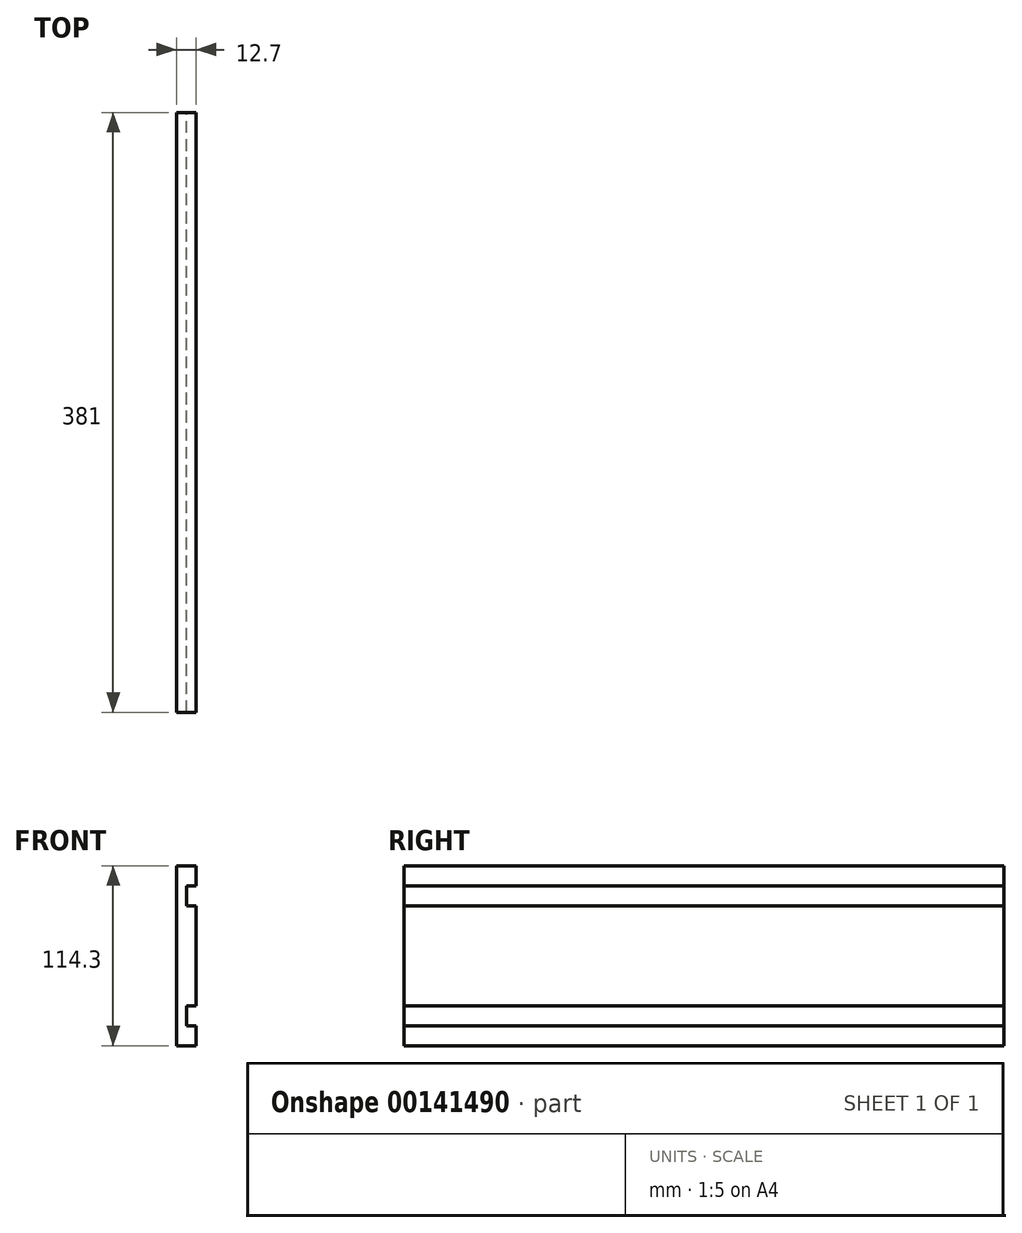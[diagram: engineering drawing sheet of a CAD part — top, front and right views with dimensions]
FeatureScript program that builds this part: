
annotation { "Feature Type Name" : "Feature", "Feature Type Description" : "" }
export const myFeature = defineFeature(function(context is Context, id is Id, definition is map)
    precondition{}
    {
        {
            var Q0;
            Q0=qCreatedBy(makeId("Front.planeOp"),FACE);
            var sketch = newSketch(context, id + "F0", { "sketchPlane" : qUnion([Q0])});
            skLineSegment(sketch, "E0.bottom", {"start": v(0, 114.3) * mm, "end": v(12.7, 114.3) * mm});
            skLineSegment(sketch, "E0.top", {"start": v(0, 0) * mm, "end": v(12.7, 0) * mm});
            skLineSegment(sketch, "E0.left", {"start": v(0, 114.3) * mm, "end": v(0, 0) * mm});
            skLineSegment(sketch, "E0.right", {"start": v(12.7, 114.3) * mm, "end": v(12.7, 101.6) * mm});
            skLineSegment(sketch, "E1.bottom", {"start": v(12.7, 25.4) * mm, "end": v(6.35, 25.4) * mm});
            skLineSegment(sketch, "E1.top", {"start": v(12.7, 12.7) * mm, "end": v(6.35, 12.7) * mm});
            skLineSegment(sketch, "E1.right", {"start": v(6.35, 25.4) * mm, "end": v(6.35, 12.7) * mm});
            skLineSegment(sketch, "E2.trimOffspring", {"start": v(12.7, 12.7) * mm, "end": v(12.7, 0) * mm});
            skLineSegment(sketch, "E3.bottom", {"start": v(12.7, 101.6) * mm, "end": v(6.35, 101.6) * mm});
            skLineSegment(sketch, "E3.top", {"start": v(12.7, 88.9) * mm, "end": v(6.35, 88.9) * mm});
            skLineSegment(sketch, "E3.right", {"start": v(6.35, 101.6) * mm, "end": v(6.35, 88.9) * mm});
            skLineSegment(sketch, "E4.trimOffspring", {"start": v(12.7, 88.9) * mm, "end": v(12.7, 25.4) * mm});
            skSolve(sketch);
        }
        {
            var Q0;
            Q0=makeQuery(id+"F0.imprint","IMPRINT",FACE,{"disambiguationData":[TD([[makeQuery(id+"F0.imprint","IMPRINT",EDGE,{"derivedFrom":sQuery(id+"F0.wireOp",EDGE,"E0.bottom")}),-1.0]])]});
            extrude(context, id + "F1", {"entities" : qUnion([Q0]), "depth" : 381 * mm});
        }
    });
